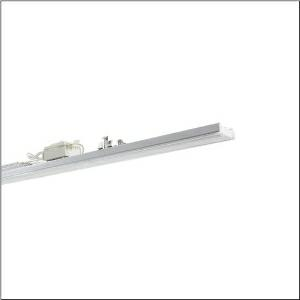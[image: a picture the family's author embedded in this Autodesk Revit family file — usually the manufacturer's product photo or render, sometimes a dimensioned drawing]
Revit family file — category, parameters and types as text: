
# Revit family: licross_r__21_recessed_mo_52tl18de445g_1bd1
name_source: partatom
category: Lighting Fixtures
units: mm (PartAtom-declared; Revit-internal decimal feet)

## family parameters
Cut with Voids When Loaded = No
Host = Face
Light Source = No
Part Type = Normal
Room Calculation Point = No
Round Connector Dimension = Use Diameter
Shared = No

## types (1)
- --- (1 x LED, 4990 lm, 29.9 W, 4000K)
    Apparent Load = 30 VA
    CIE Flux Codes = 79 95 99 100 100
    Color Rendering = 80
    Color Temperature = 4000K
    Default Elevation = 1800 mm
    Description = Licross® 21 Recessed MO, luminaire insert, of sheet steel, galvanised, coil coated, white, length: 750mm, width: 66mm, height: 67mm, LED rated luminous flux: 4.990lm, light colour: 840, control gear: DALI 2, with plug, 5-pole, with phase selection, mains connection: 220..240V, AC, 50/60Hz, rated input power: 30W, internal wiring halogen-free, primary light control with lens, of plastic, primary optical cover: cover, of PMMA, light emission: direct distribution, primary light characteristic: symmetric, protection rating (complete): IP40, insulation class (complete): insulation class I (protective earthing), certification: CE, ENEC, VDE, UKCA, protection symbol: D if used in an environment without relevant dust loads with corresponding accessories, impact resistance: IK06, permissible ambient temperature for indoor applications: -25..+35°C, corresponds to IFS (International Featured Standards) requirements for safety and quality in the food industry, reducing of maximum allowable ambient temperature of 5°C with ceiling mounting, LABS conformity tested according to VDMA 24364:2018-05, packaging unit: 1 piece
    Height = 58 mm
    Lamp = 1 x LED
    Lamp Light Flux = 4990 lm
    Lamp Power = 29.9 W
    Lamp count = 1
    Length = 750 mm
    Luminous efficacy = 167 lm/W
    Manufacturer = Siteco
    ModVariant = No
    Model = 52TL18DE445G
    Mounting Place = Ceiling
    Mounting Type = Pendant
    Number of Poles = 1
    OnlyDefault = Yes
    Power Factor = 1
    Product Name = Licross® 21 Recessed MO
    Product group = luminaire insert | ceiling pendant
    ProductGroupID = 902
    Protection Class = Protection class I
    Protection Degree = IP 40
    RLX_Detail_Level = 1
    RLX_Emergency_Light_Flux = 0 lm
    RLX_Emergency_Type = 0
    RLX_Emergency_Type_DB = No
    RlxData = <blob elided: 28881 chars, md5=e3223446>
    Socket = socket
    Standby Power = 0 W
    System Light Flux = 4990 lm
    System Power = 30 W
    Type Comments = factory setting: luminous flux: 100 % | dim-lin: 254 | 390 mA
    Type Image = l_1296930.jpg
    URL = http://relux.com
    VarID = @adj_147613
    Voltage = 0 V
    Weight = 0.00 kg
    Width = 66 mm

## geometry (parser evidence)
native form markers: Blend x4, Sweep x8
no freeform markers — native parametric forms only
